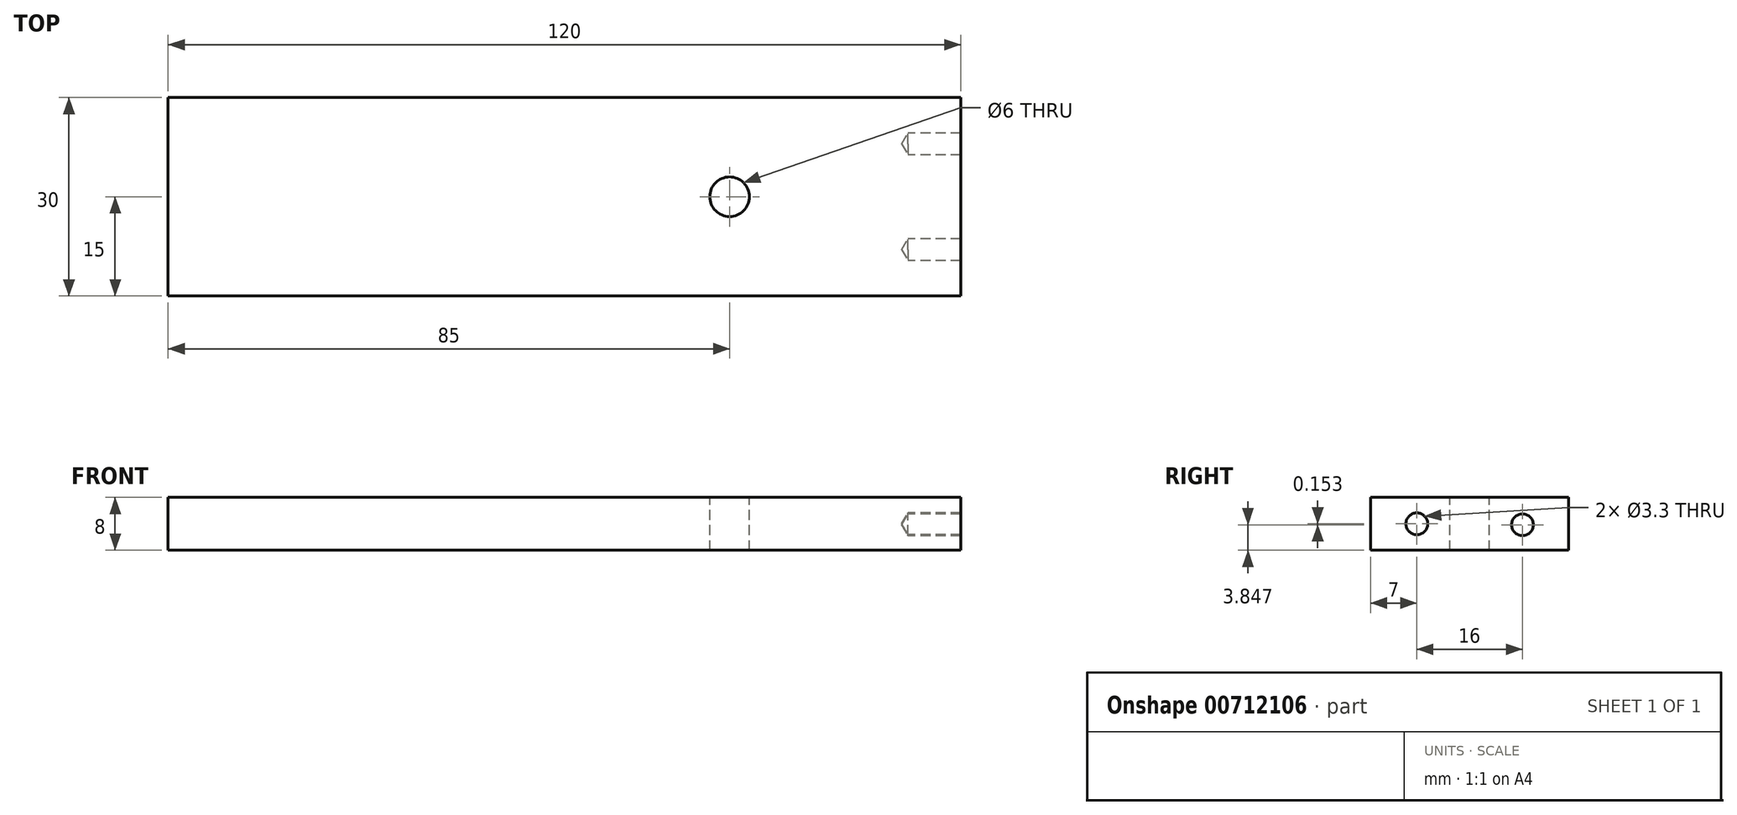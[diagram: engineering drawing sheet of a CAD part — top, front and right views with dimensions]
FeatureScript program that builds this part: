
annotation { "Feature Type Name" : "Feature", "Feature Type Description" : "" }
export const myFeature = defineFeature(function(context is Context, id is Id, definition is map)
    precondition{}
    {
        {
            var Q0;
            Q0=qCreatedBy(makeId("Top.planeOp"),FACE);
            var sketch = newSketch(context, id + "F0", { "sketchPlane" : qUnion([Q0])});
            skLineSegment(sketch, "E0.bottom", {"start": v(60, -15) * mm, "end": v(-60, -15) * mm});
            skLineSegment(sketch, "E0.top", {"start": v(60, 15) * mm, "end": v(-60, 15) * mm});
            skLineSegment(sketch, "E0.left", {"start": v(60, -15) * mm, "end": v(60, 15) * mm});
            skLineSegment(sketch, "E0.right", {"start": v(-60, -15) * mm, "end": v(-60, 15) * mm});
            skPoint(sketch, "E0.middle", {"position": v(0, 0) * mm});
            skSolve(sketch);
        }
        {
            var Q0;
            Q0=makeQuery(id+"F0.imprint","IMPRINT",FACE,{"disambiguationData":[TD([[makeQuery(id+"F0.imprint","IMPRINT",EDGE,{"derivedFrom":sQuery(id+"F0.wireOp",EDGE,"E0.bottom")}),-1.0]])]});
            extrude(context, id + "F1", {"entities" : qUnion([Q0]), "depth" : 8 * mm, "offsetDistance" : 25 * mm, "symmetric" : true});
        }
        {
            var Q0;
            Q0=makeQuery(id+"F1.opExtrude","CAP_FACE",FACE,{"disambiguationData":[OSD([sQuery(id+"F0.wireOp",EDGE,"E0.bottom"),sQuery(id+"F0.wireOp",EDGE,"E0.top"),sQuery(id+"F0.wireOp",EDGE,"E0.left"),sQuery(id+"F0.wireOp",EDGE,"E0.right")])],"isStart":false});
            var sketch = newSketch(context, id + "F2", { "sketchPlane" : qUnion([Q0])});
            skLineSegment(sketch, "E1", {"start": v(25, 46.87) * mm, "end": v(25, -40.26) * mm, "construction": true});
            skCircle(sketch, "E2", {"center": v(25, 0) * mm, "radius": 3 * mm});
            skSolve(sketch);
        }
        {
            var Q0;
            Q0=makeQuery(id+"F2.imprint","IMPRINT",FACE,{"disambiguationData":[TD([[makeQuery(id+"F2.imprint","IMPRINT",EDGE,{"derivedFrom":sQuery(id+"F2.wireOp",EDGE,"E2")}),1.0]])]});
            var Q1;
            Q1=sQuery(id+"F2.wireOp",EDGE,"E2");
            extrude(context, id + "F3", {"entities" : qUnion([Q0]), "operationType" : NewBodyOperationType.REMOVE, "surfaceEntities" : qUnion([Q1]), "oppositeDirection" : true, "depth" : 25 * mm, "offsetDistance" : 25 * mm});
        }
        {
            var Q0;
            Q0=makeQuery(id+"F1.opExtrude","SWEPT_FACE",FACE,{"disambiguationData":[OSD([sQuery(id+"F0.wireOp",EDGE,"E0.left")])]});
            var sketch = newSketch(context, id + "F4", { "sketchPlane" : qUnion([Q0])});
            skLineSegment(sketch, "E3", {"start": v(0, 17.36) * mm, "end": v(0, -17.66) * mm, "construction": true});
            skLineSegment(sketch, "E4.0", {"start": v(-8, 17.36) * mm, "end": v(-8, -17.66) * mm, "construction": true});
            skLineSegment(sketch, "E5.MirrorCS", {"start": v(8, 17.36) * mm, "end": v(8, -17.66) * mm, "construction": true});
            skPoint(sketch, "E6", {"position": v(-8, 0) * mm});
            skPoint(sketch, "E7", {"position": v(8, -0.15) * mm});
            skSolve(sketch);
        }
        {
            var Q0;
            Q0=sQuery(id+"F4.wireOp",VERTEX,"E6");
            var Q1;
            Q1=sQuery(id+"F4.wireOp",VERTEX,"E7");
            var Q2;
            Q2=makeQuery(id+"F1.opExtrude","SWEPT_BODY",BODY,{"disambiguationData":[OSD([sQuery(id+"F0.wireOp",EDGE,"E0.bottom"),sQuery(id+"F0.wireOp",EDGE,"E0.top"),sQuery(id+"F0.wireOp",EDGE,"E0.left"),sQuery(id+"F0.wireOp",EDGE,"E0.right")])]});
            hole(context, id + "F5", {"style" : HoleStyle.SIMPLE, "endStyle" : HoleEndStyle.BLIND, "standardTappedOrClearance" : lookupTablePath({ "standard" : "ISO", "fit" : "Normal", "size" : "M3", "type" : "Clearance" }), "standardBlindInLast" : lookupTablePath({ "fit" : "Standard", "standard" : "ISO", "size" : "M3", "type" : "Clearance" }), "holeDiameter" : 3.3 * mm, "majorDiameter" : 5 * mm, "holeDepth" : 8 * mm, "tappedDepth" : 12 * mm, "tapClearance" : 3, "locations" : qUnion([Q0, Q1]), "scope" : qUnion([Q2]), "startStyle" : HoleStartStyle.PART});
        }
    });
